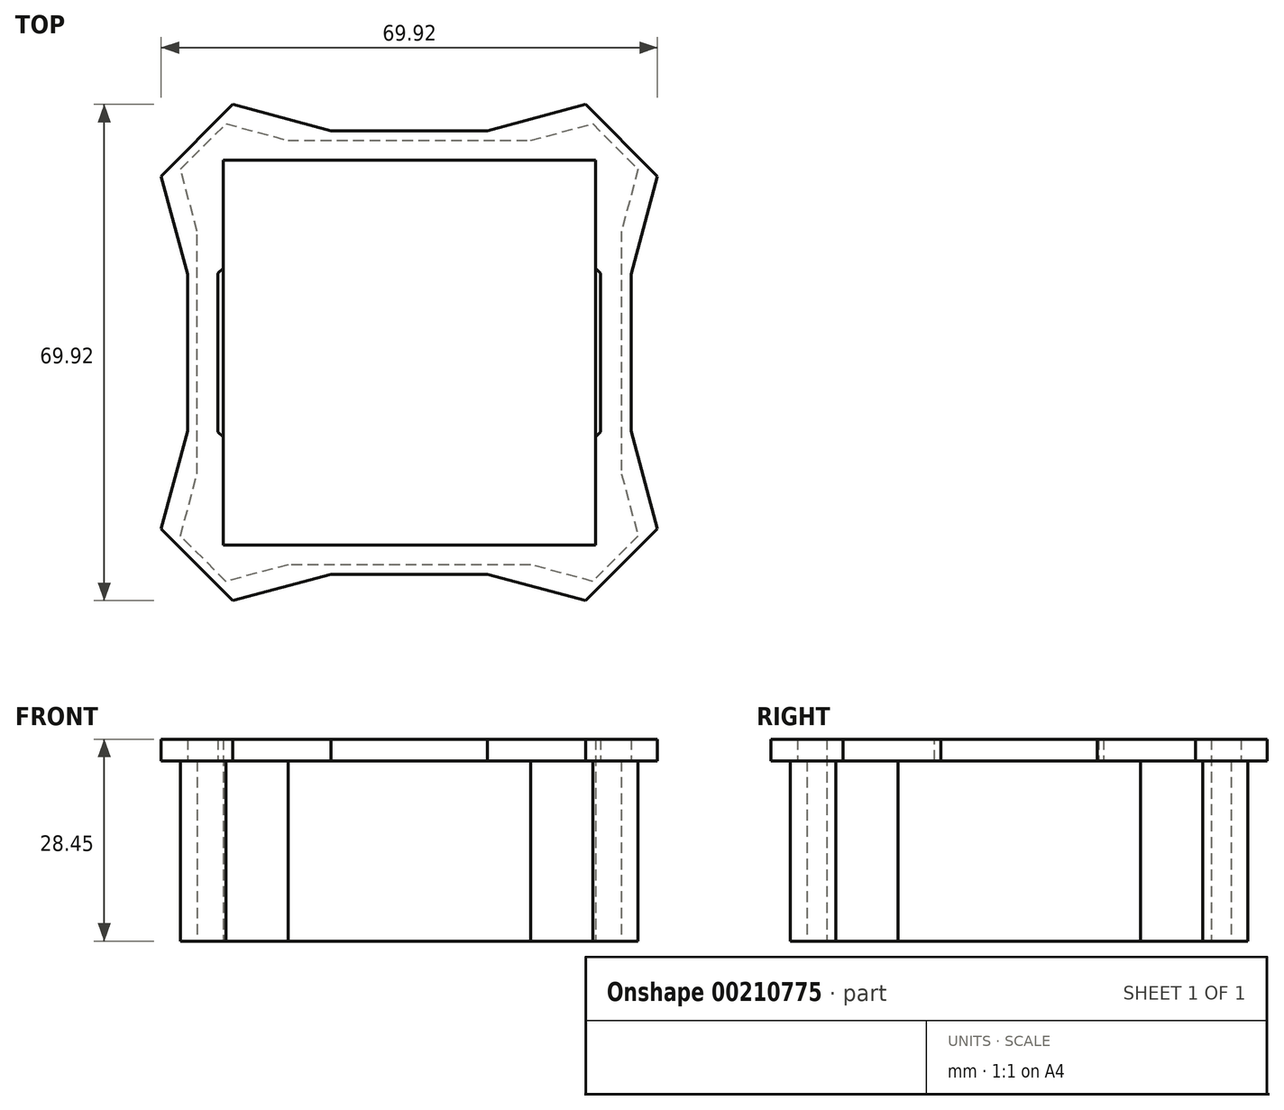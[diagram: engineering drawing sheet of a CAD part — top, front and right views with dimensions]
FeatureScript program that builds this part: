
annotation { "Feature Type Name" : "Feature", "Feature Type Description" : "" }
export const myFeature = defineFeature(function(context is Context, id is Id, definition is map)
    precondition{}
    {
        {
            var Q0;
            Q0=qCreatedBy(makeId("Top.planeOp"),FACE);
            cPlane(context, id + "F0", {"entities" : qUnion([Q0]), "cplaneType" : CPlaneType.OFFSET, "offset" : 31.24 * mm, "width" : 152.4 * mm, "height" : 152.4 * mm});
        }
        {
            var Q0;
            Q0=qCreatedBy(id+"F0.planeOp",FACE);
            cPlane(context, id + "F1", {"entities" : qUnion([Q0]), "cplaneType" : CPlaneType.OFFSET, "offset" : 19.05 * mm, "width" : 152.4 * mm, "height" : 152.4 * mm});
        }
        {
            var Q0;
            Q0=qCreatedBy(id+"F1.planeOp",FACE);
            var sketch = newSketch(context, id + "F2", { "sketchPlane" : qUnion([Q0])});
            skPoint(sketch, "E0.0.midPoint", {"position": v(0, 33.22) * mm});
            skCircle(sketch, "E1.cCircle", {"center": v(-23.49, -23.49) * mm, "radius": 7.84 * mm, "construction": true});
            skLineSegment(sketch, "E1.0", {"start": v(-25.83, -32.23) * mm, "end": v(-32.23, -25.83) * mm});
            skLineSegment(sketch, "E1.1", {"start": v(-32.23, -25.83) * mm, "end": v(-29.89, -17.09) * mm});
            skLineSegment(sketch, "E1.2", {"start": v(-29.89, -17.09) * mm, "end": v(-21.15, -14.75) * mm});
            skLineSegment(sketch, "E1.3", {"start": v(-21.15, -14.75) * mm, "end": v(-14.75, -21.15) * mm});
            skLineSegment(sketch, "E1.4", {"start": v(-14.75, -21.15) * mm, "end": v(-17.09, -29.89) * mm});
            skLineSegment(sketch, "E1.5", {"start": v(-17.09, -29.89) * mm, "end": v(-25.83, -32.23) * mm});
            skPoint(sketch, "E1.0.midPoint", {"position": v(-29.03, -29.03) * mm});
            skCircle(sketch, "E2.cCircle", {"center": v(23.49, -23.49) * mm, "radius": 7.84 * mm, "construction": true});
            skLineSegment(sketch, "E2.0", {"start": v(32.23, -25.83) * mm, "end": v(25.83, -32.23) * mm});
            skLineSegment(sketch, "E2.1", {"start": v(25.83, -32.23) * mm, "end": v(17.09, -29.89) * mm});
            skLineSegment(sketch, "E2.2", {"start": v(17.09, -29.89) * mm, "end": v(14.75, -21.15) * mm});
            skLineSegment(sketch, "E2.3", {"start": v(14.75, -21.15) * mm, "end": v(21.15, -14.75) * mm});
            skLineSegment(sketch, "E2.4", {"start": v(21.15, -14.75) * mm, "end": v(29.89, -17.09) * mm});
            skLineSegment(sketch, "E2.5", {"start": v(29.89, -17.09) * mm, "end": v(32.23, -25.83) * mm});
            skPoint(sketch, "E2.0.midPoint", {"position": v(29.03, -29.03) * mm});
            skCircle(sketch, "E3.cCircle", {"center": v(23.49, 23.49) * mm, "radius": 7.84 * mm, "construction": true});
            skLineSegment(sketch, "E3.0", {"start": v(25.83, 32.23) * mm, "end": v(32.23, 25.83) * mm});
            skLineSegment(sketch, "E3.1", {"start": v(32.23, 25.83) * mm, "end": v(29.89, 17.09) * mm});
            skLineSegment(sketch, "E3.2", {"start": v(29.89, 17.09) * mm, "end": v(21.15, 14.75) * mm});
            skLineSegment(sketch, "E3.3", {"start": v(21.15, 14.75) * mm, "end": v(14.75, 21.15) * mm});
            skLineSegment(sketch, "E3.4", {"start": v(14.75, 21.15) * mm, "end": v(17.09, 29.89) * mm});
            skLineSegment(sketch, "E3.5", {"start": v(17.09, 29.89) * mm, "end": v(25.83, 32.23) * mm});
            skPoint(sketch, "E3.0.midPoint", {"position": v(29.03, 29.03) * mm});
            skCircle(sketch, "E4.cCircle", {"center": v(-23.49, 23.49) * mm, "radius": 7.84 * mm, "construction": true});
            skLineSegment(sketch, "E4.0", {"start": v(-32.23, 25.83) * mm, "end": v(-25.83, 32.23) * mm});
            skLineSegment(sketch, "E4.1", {"start": v(-25.83, 32.23) * mm, "end": v(-17.09, 29.89) * mm});
            skLineSegment(sketch, "E4.2", {"start": v(-17.09, 29.89) * mm, "end": v(-14.75, 21.15) * mm});
            skLineSegment(sketch, "E4.3", {"start": v(-14.75, 21.15) * mm, "end": v(-21.15, 14.75) * mm});
            skLineSegment(sketch, "E4.4", {"start": v(-21.15, 14.75) * mm, "end": v(-29.89, 17.09) * mm});
            skLineSegment(sketch, "E4.5", {"start": v(-29.89, 17.09) * mm, "end": v(-32.23, 25.83) * mm});
            skPoint(sketch, "E4.0.midPoint", {"position": v(-29.03, 29.03) * mm});
            skLineSegment(sketch, "E5", {"start": v(-21.15, -14.75) * mm, "end": v(-21.15, 14.75) * mm});
            skLineSegment(sketch, "E6", {"start": v(-14.75, 21.15) * mm, "end": v(14.75, 21.15) * mm});
            skLineSegment(sketch, "E7", {"start": v(-14.75, -21.15) * mm, "end": v(14.75, -21.15) * mm});
            skLineSegment(sketch, "E8", {"start": v(21.15, -14.75) * mm, "end": v(21.15, 14.75) * mm});
            skLineSegment(sketch, "E9", {"start": v(17.09, -29.89) * mm, "end": v(-17.09, -29.89) * mm});
            skLineSegment(sketch, "E10", {"start": v(-29.89, -17.09) * mm, "end": v(-29.89, 17.09) * mm});
            skLineSegment(sketch, "E11", {"start": v(-17.09, 29.89) * mm, "end": v(17.09, 29.89) * mm});
            skLineSegment(sketch, "E12", {"start": v(29.89, 17.09) * mm, "end": v(29.89, -17.09) * mm});
            skSolve(sketch);
        }
        {
            var Q0;
            Q0=qCreatedBy(id+"F1.planeOp",FACE);
            cPlane(context, id + "F3", {"entities" : qUnion([Q0]), "cplaneType" : CPlaneType.OFFSET, "offset" : 25.4 * mm, "width" : 152.4 * mm, "height" : 152.4 * mm});
        }
        {
            var Q0;
            Q0=qCreatedBy(id+"F3.planeOp",FACE);
            var sketch = newSketch(context, id + "F4", { "sketchPlane" : qUnion([Q0])});
            skLineSegment(sketch, "E13.0", {"start": v(-12.38, 29.9) * mm, "end": v(12.38, 29.9) * mm});
            skLineSegment(sketch, "E13.2", {"start": v(29.9, 12.38) * mm, "end": v(29.9, -12.38) * mm});
            skLineSegment(sketch, "E13.4", {"start": v(12.38, -29.9) * mm, "end": v(-12.38, -29.9) * mm});
            skLineSegment(sketch, "E13.6", {"start": v(-29.9, -12.38) * mm, "end": v(-29.9, 12.38) * mm});
            skPoint(sketch, "E13.0.midPoint", {"position": v(0, 29.9) * mm});
            skLineSegment(sketch, "E14.0", {"start": v(-34.96, 24.84) * mm, "end": v(-24.84, 34.96) * mm});
            skLineSegment(sketch, "E14.1", {"start": v(-24.84, 34.96) * mm, "end": v(-11.03, 31.25) * mm});
            skLineSegment(sketch, "E14.3", {"start": v(-7.33, 17.44) * mm, "end": v(-17.44, 7.33) * mm});
            skLineSegment(sketch, "E14.5", {"start": v(-31.25, 11.03) * mm, "end": v(-34.96, 24.84) * mm});
            skPoint(sketch, "E14.0.midPoint", {"position": v(-29.9, 29.9) * mm});
            skLineSegment(sketch, "E15.0", {"start": v(24.84, 34.96) * mm, "end": v(34.96, 24.84) * mm});
            skLineSegment(sketch, "E15.1", {"start": v(34.96, 24.84) * mm, "end": v(31.25, 11.03) * mm});
            skLineSegment(sketch, "E15.3", {"start": v(17.44, 7.33) * mm, "end": v(7.33, 17.44) * mm});
            skLineSegment(sketch, "E15.5", {"start": v(11.03, 31.25) * mm, "end": v(24.84, 34.96) * mm});
            skPoint(sketch, "E15.0.midPoint", {"position": v(29.9, 29.9) * mm});
            skLineSegment(sketch, "E16.0", {"start": v(34.96, -24.84) * mm, "end": v(24.84, -34.96) * mm});
            skLineSegment(sketch, "E16.1", {"start": v(24.84, -34.96) * mm, "end": v(11.03, -31.25) * mm});
            skLineSegment(sketch, "E16.3", {"start": v(7.33, -17.44) * mm, "end": v(17.44, -7.33) * mm});
            skLineSegment(sketch, "E16.5", {"start": v(31.25, -11.03) * mm, "end": v(34.96, -24.84) * mm});
            skPoint(sketch, "E16.0.midPoint", {"position": v(29.9, -29.9) * mm});
            skLineSegment(sketch, "E17.0", {"start": v(-24.84, -34.96) * mm, "end": v(-34.96, -24.84) * mm});
            skLineSegment(sketch, "E17.1", {"start": v(-34.96, -24.84) * mm, "end": v(-31.25, -11.03) * mm});
            skLineSegment(sketch, "E17.3", {"start": v(-17.44, -7.33) * mm, "end": v(-7.33, -17.44) * mm});
            skLineSegment(sketch, "E17.5", {"start": v(-11.03, -31.25) * mm, "end": v(-24.84, -34.96) * mm});
            skPoint(sketch, "E17.0.midPoint", {"position": v(-29.9, -29.9) * mm});
            skLineSegment(sketch, "E18", {"start": v(-11.03, -31.25) * mm, "end": v(11.03, -31.25) * mm});
            skLineSegment(sketch, "E19", {"start": v(31.25, -11.03) * mm, "end": v(31.25, 11.03) * mm});
            skLineSegment(sketch, "E20", {"start": v(-11.03, 31.25) * mm, "end": v(11.03, 31.25) * mm});
            skLineSegment(sketch, "E21", {"start": v(-31.25, 11.03) * mm, "end": v(-31.25, -11.03) * mm});
            skLineSegment(sketch, "E22", {"start": v(-7.33, -17.44) * mm, "end": v(7.33, -17.44) * mm});
            skLineSegment(sketch, "E23", {"start": v(17.44, -7.33) * mm, "end": v(17.44, 7.33) * mm});
            skLineSegment(sketch, "E24", {"start": v(7.33, 17.44) * mm, "end": v(-7.33, 17.44) * mm});
            skCircle(sketch, "E25.cCircle", {"center": v(0, 0) * mm, "radius": 21.51 * mm, "construction": true});
            skPoint(sketch, "E25.cCircle.perimeterSnap0", {"position": v(17.44, 0) * mm});
            skLineSegment(sketch, "E25.0", {"start": v(21.51, 8.91) * mm, "end": v(21.51, -8.91) * mm});
            skLineSegment(sketch, "E25.1", {"start": v(21.51, -8.91) * mm, "end": v(8.91, -21.51) * mm});
            skLineSegment(sketch, "E25.2", {"start": v(8.91, -21.51) * mm, "end": v(-8.91, -21.51) * mm});
            skLineSegment(sketch, "E25.4", {"start": v(-21.51, -8.91) * mm, "end": v(-21.51, 8.91) * mm});
            skLineSegment(sketch, "E25.5", {"start": v(-21.51, 8.91) * mm, "end": v(-8.91, 21.51) * mm});
            skLineSegment(sketch, "E25.6", {"start": v(-8.91, 21.51) * mm, "end": v(8.91, 21.51) * mm});
            skLineSegment(sketch, "E25.7", {"start": v(8.91, 21.51) * mm, "end": v(21.51, 8.91) * mm});
            skPoint(sketch, "E25.0.midPoint", {"position": v(21.51, 0) * mm});
            skPoint(sketch, "E25.0.midPoint.positionSnap0", {"position": v(17.44, 0) * mm});
            skCircle(sketch, "E26.cCircle", {"center": v(0, 0) * mm, "radius": 26.95 * mm, "construction": true});
            skPoint(sketch, "E26.cCircle.perimeterSnap0", {"position": v(0, 21.51) * mm});
            skLineSegment(sketch, "E26.0", {"start": v(-11.16, 26.95) * mm, "end": v(11.16, 26.95) * mm});
            skLineSegment(sketch, "E26.1", {"start": v(11.16, 26.95) * mm, "end": v(26.95, 11.16) * mm});
            skLineSegment(sketch, "E26.2", {"start": v(26.95, 11.16) * mm, "end": v(26.95, -11.16) * mm});
            skLineSegment(sketch, "E26.3", {"start": v(26.95, -11.16) * mm, "end": v(11.16, -26.95) * mm});
            skLineSegment(sketch, "E26.4", {"start": v(11.16, -26.95) * mm, "end": v(-11.16, -26.95) * mm});
            skLineSegment(sketch, "E26.5", {"start": v(-11.16, -26.95) * mm, "end": v(-26.95, -11.16) * mm});
            skLineSegment(sketch, "E26.6", {"start": v(-26.95, -11.16) * mm, "end": v(-26.95, 11.16) * mm});
            skLineSegment(sketch, "E26.7", {"start": v(-26.95, 11.16) * mm, "end": v(-11.16, 26.95) * mm});
            skPoint(sketch, "E26.0.midPoint", {"position": v(0, 26.95) * mm});
            skPoint(sketch, "E26.0.midPoint.positionSnap0", {"position": v(0, 21.51) * mm});
            skSolve(sketch);
        }
        {
            var Q0;
            Q0 = qSketchRegion(id + "F2", true);
            extrude(context, id + "F5", {"entities" : qUnion([Q0]), "depth" : 25.4 * mm});
        }
        {
            var Q0;
            Q0 = qSketchRegion(id + "F4", true);
            extrude(context, id + "F6", {"entities" : qUnion([Q0]), "operationType" : NewBodyOperationType.ADD, "depth" : 3.05 * mm});
        }
        {
            var Q0;
            Q0=qCreatedBy(id+"F1.planeOp",FACE);
            var sketch = newSketch(context, id + "F7", { "sketchPlane" : qUnion([Q0])});
            skLineSegment(sketch, "E27.bottom", {"start": v(-26.22, 27.09) * mm, "end": v(26.22, 27.09) * mm});
            skLineSegment(sketch, "E27.top", {"start": v(-26.22, -27.09) * mm, "end": v(26.22, -27.09) * mm});
            skLineSegment(sketch, "E27.left", {"start": v(-26.22, 27.09) * mm, "end": v(-26.22, -27.09) * mm});
            skLineSegment(sketch, "E27.right", {"start": v(26.22, 27.09) * mm, "end": v(26.22, -27.09) * mm});
            skPoint(sketch, "E27.middle", {"position": v(0, 0) * mm});
            skSolve(sketch);
        }
        {
            var Q0;
            Q0 = qSketchRegion(id + "F7", true);
            extrude(context, id + "F8", {"entities" : qUnion([Q0]), "operationType" : NewBodyOperationType.REMOVE, "depth" : 88.65 * mm});
        }
    });
